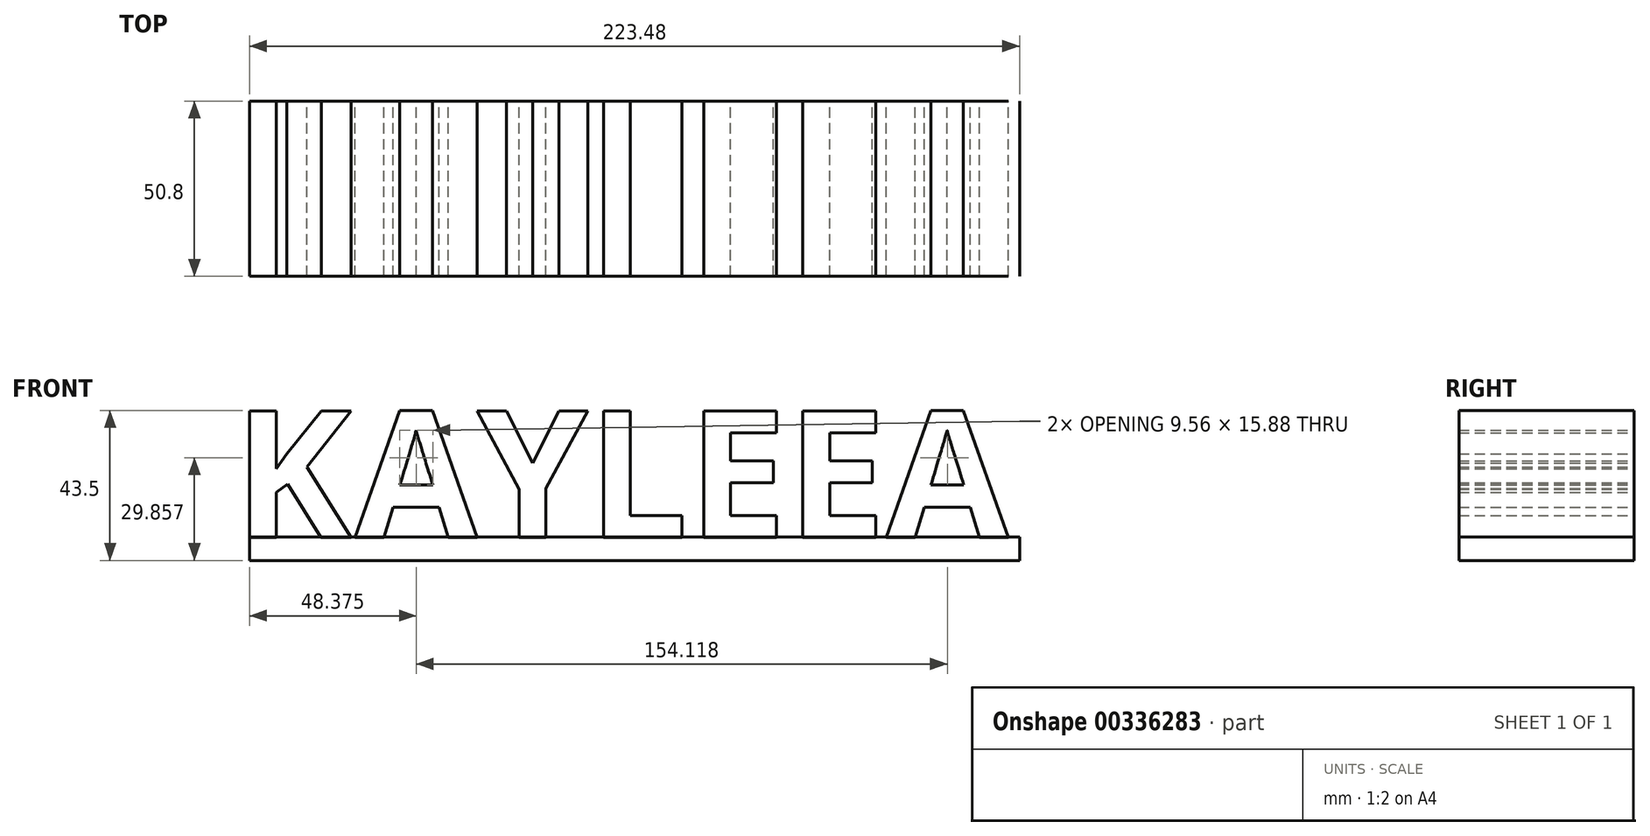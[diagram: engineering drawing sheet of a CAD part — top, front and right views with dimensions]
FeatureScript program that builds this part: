
annotation { "Feature Type Name" : "Feature", "Feature Type Description" : "" }
export const myFeature = defineFeature(function(context is Context, id is Id, definition is map)
    precondition{}
    {
        {
            var Q0;
            Q0=qCreatedBy(makeId("Front.planeOp"),FACE);
            var sketch = newSketch(context, id + "F0", { "sketchPlane" : qUnion([Q0])});
            skText(sketch, "E0", { "text": "KAYLEEA", "fontName": "OpenSans-Bold.ttf"});
            const initialGuessF0  = {"E0": [-0.09428, -0.00157, 1, 0, 0.037]};
            skSetInitialGuess(sketch, initialGuessF0);
            skSolve(sketch);
        }
        {
            var Q0;
            Q0=qCreatedBy(makeId("Front.planeOp"),FACE);
            var sketch = newSketch(context, id + "F1", { "sketchPlane" : qUnion([Q0])});
            skLineSegment(sketch, "E1.bottom", {"start": v(-89.65, -1.39) * mm, "end": v(133.82, -1.39) * mm});
            skLineSegment(sketch, "E1.top", {"start": v(-89.65, -8.23) * mm, "end": v(133.82, -8.23) * mm});
            skLineSegment(sketch, "E1.left", {"start": v(-89.65, -1.39) * mm, "end": v(-89.65, -8.23) * mm});
            skLineSegment(sketch, "E1.right", {"start": v(133.82, -1.39) * mm, "end": v(133.82, -8.23) * mm});
            skSolve(sketch);
        }
        {
            var Q0;
            Q0 = qSketchRegion(id + "F0", true);
            var Q1;
            Q1 = qSketchRegion(id + "F1", true);
            extrude(context, id + "F2", {"entities" : qUnion([Q0, Q1]), "endBound" : BoundingType.SYMMETRIC, "depth" : 50.8 * mm});
        }
    });
